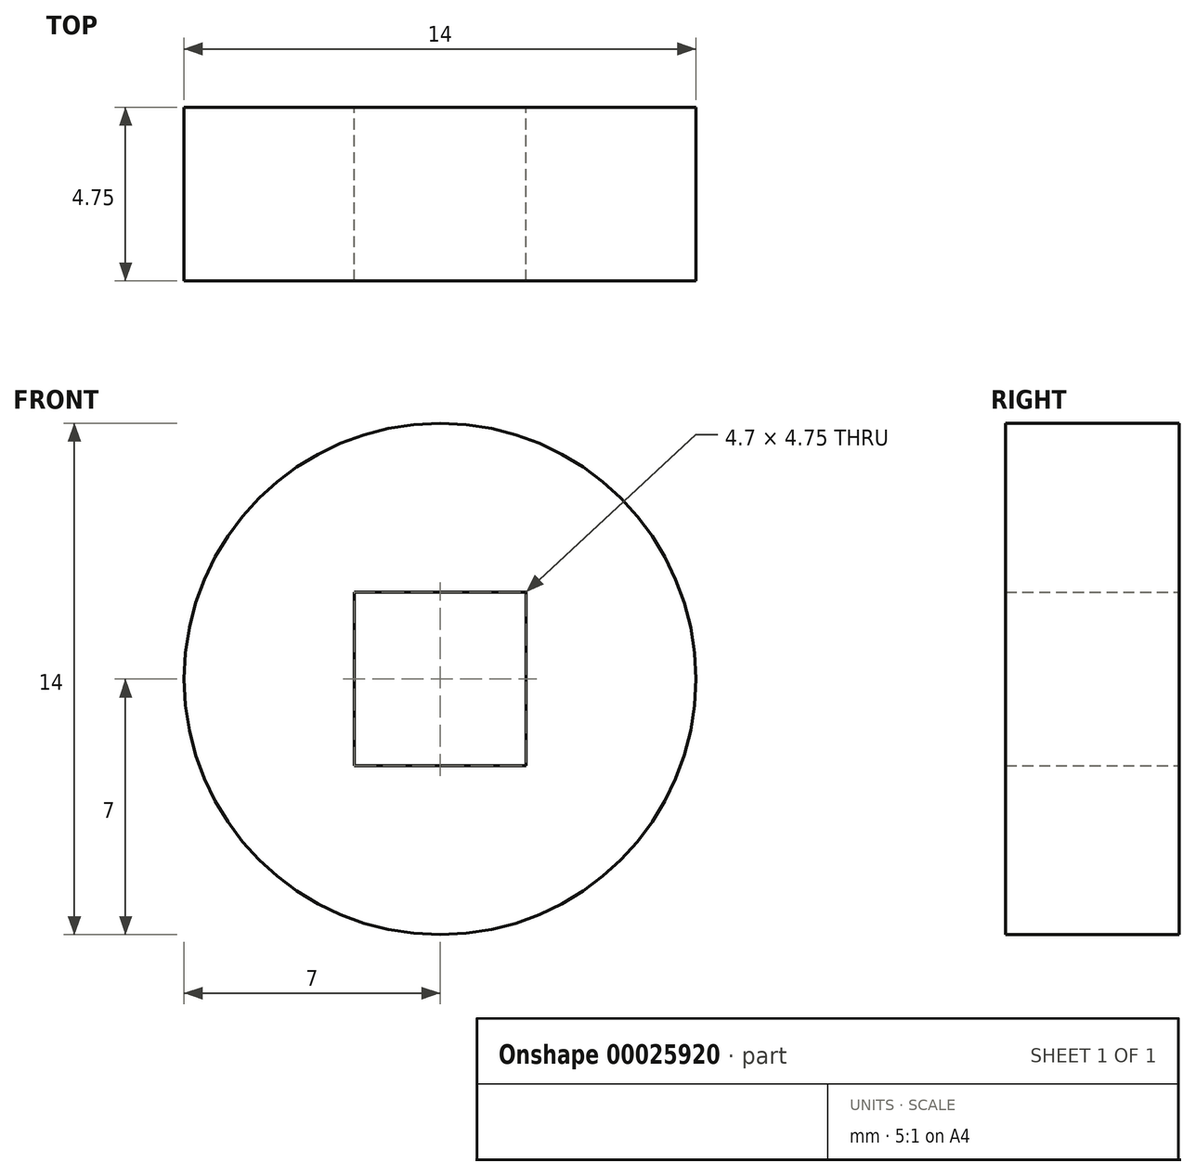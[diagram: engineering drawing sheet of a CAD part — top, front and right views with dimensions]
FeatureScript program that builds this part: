
annotation { "Feature Type Name" : "Feature", "Feature Type Description" : "" }
export const myFeature = defineFeature(function(context is Context, id is Id, definition is map)
    precondition{}
    {
        {
            var Q0;
            Q0=qCreatedBy(makeId("Front.planeOp"),FACE);
            var sketch = newSketch(context, id + "F0", { "sketchPlane" : qUnion([Q0])});
            skCircle(sketch, "E0", {"center": v(0, 0) * mm, "radius": 7 * mm});
            skLineSegment(sketch, "E1.rect.bottom", {"start": v(2.35, 2.38) * mm, "end": v(-2.35, 2.38) * mm});
            skLineSegment(sketch, "E1.rect.top", {"start": v(2.35, -2.38) * mm, "end": v(-2.35, -2.38) * mm});
            skLineSegment(sketch, "E1.rect.left", {"start": v(2.35, 2.38) * mm, "end": v(2.35, -2.38) * mm});
            skLineSegment(sketch, "E1.rect.right", {"start": v(-2.35, 2.38) * mm, "end": v(-2.35, -2.38) * mm});
            skSolve(sketch);
        }
        {
            var Q0;
            Q0=makeQuery(id+"F0.imprint","IMPRINT",FACE,{"disambiguationData":[TD([[makeQuery(id+"F0.imprint","IMPRINT",EDGE,{"derivedFrom":sQuery(id+"F0.wireOp",EDGE,"5f4a554a-107a-4ad8-bc78-8fd444699d9d")}),-1.0]])]});
            var Q1;
            Q1=makeQuery(id+"F0.imprint","IMPRINT",FACE,{"disambiguationData":[TD([[makeQuery(id+"F0.imprint","IMPRINT",EDGE,{"derivedFrom":sQuery(id+"F0.wireOp",EDGE,"E0")}),1.0]])]});
            extrude(context, id + "F1", {"entities" : qUnion([Q0, Q1]), "depth" : 4.75 * mm});
        }
    });
